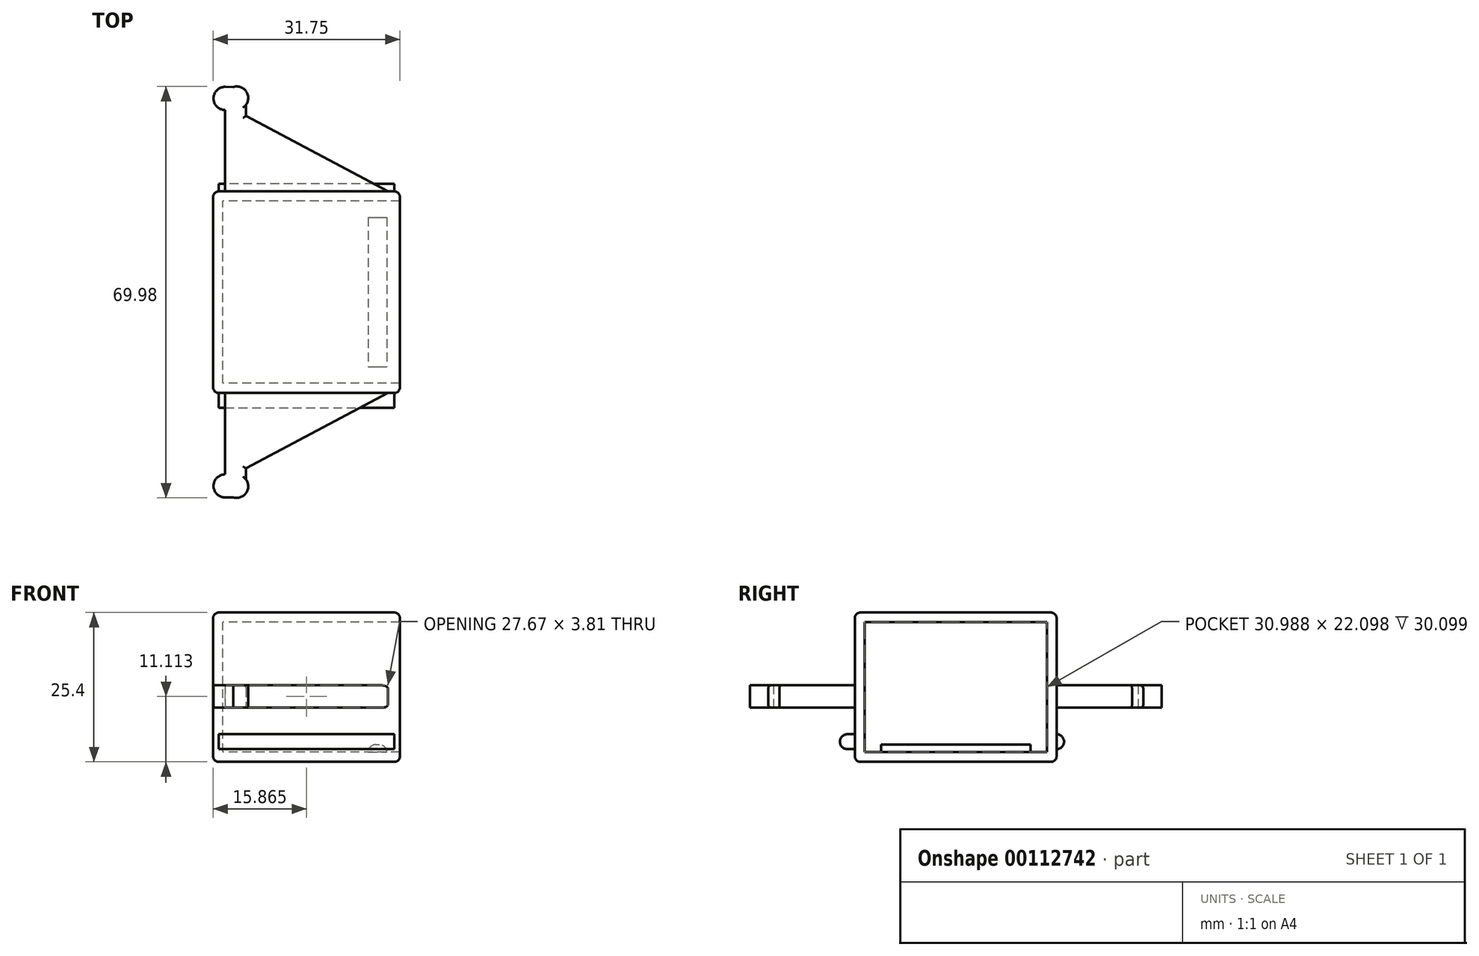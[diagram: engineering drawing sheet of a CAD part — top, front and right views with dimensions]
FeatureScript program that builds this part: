
annotation { "Feature Type Name" : "Feature", "Feature Type Description" : "" }
export const myFeature = defineFeature(function(context is Context, id is Id, definition is map)
    precondition{}
    {
        {
            var Q0;
            Q0=qCreatedBy(makeId("Right.planeOp"),FACE);
            var sketch = newSketch(context, id + "F0", { "sketchPlane" : qUnion([Q0])});
            skLineSegment(sketch, "E0.bottom", {"start": v(-17.14, 0) * mm, "end": v(17.15, 0) * mm});
            skLineSegment(sketch, "E0.top", {"start": v(-17.15, 25.4) * mm, "end": v(17.14, 25.4) * mm});
            skLineSegment(sketch, "E0.left", {"start": v(-17.14, 0) * mm, "end": v(-17.15, 25.4) * mm});
            skLineSegment(sketch, "E0.right", {"start": v(17.15, 0) * mm, "end": v(17.14, 25.4) * mm});
            skPoint(sketch, "E0.middle", {"position": v(0, 12.7) * mm});
            skLineSegment(sketch, "E1.0", {"start": v(16.26, 0.89) * mm, "end": v(16.26, 24.51) * mm, "construction": true});
            skLineSegment(sketch, "E1.1", {"start": v(-16.26, 0.89) * mm, "end": v(16.26, 0.89) * mm, "construction": true});
            skLineSegment(sketch, "E1.2", {"start": v(-16.26, 0.89) * mm, "end": v(-16.26, 24.51) * mm, "construction": true});
            skLineSegment(sketch, "E1.3", {"start": v(-16.26, 24.51) * mm, "end": v(16.26, 24.51) * mm, "construction": true});
            skSolve(sketch);
        }
        {
            var Q0;
            Q0=makeQuery(id+"F0.imprint","IMPRINT",FACE,{"disambiguationData":[TD([[makeQuery(id+"F0.imprint","IMPRINT",EDGE,{"derivedFrom":sQuery(id+"F0.wireOp",EDGE,"E1.0")}),1.0]])]});
            var Q1;
            Q1=makeQuery(id+"F0.imprint","IMPRINT",FACE,{"disambiguationData":[TD([[makeQuery(id+"F0.imprint","IMPRINT",EDGE,{"derivedFrom":sQuery(id+"F0.wireOp",EDGE,"E0.bottom")}),1.0]])]});
            extrude(context, id + "F1", {"entities" : qUnion([Q0, Q1]), "depth" : 31.75 * mm});
        }
        {
            var Q0;
            Q0=makeQuery(id+"F1.opExtrude","CAP_FACE",FACE,{"disambiguationData":[OSD([sQuery(id+"F0.wireOp",EDGE,"E0.bottom"),sQuery(id+"F0.wireOp",EDGE,"E0.top"),sQuery(id+"F0.wireOp",EDGE,"E0.left"),sQuery(id+"F0.wireOp",EDGE,"E0.right")])],"isStart":false});
            shell(context, id + "F2", {"entities" : qUnion([Q0]), "thickness" : 1.65 * mm});
        }
        {
            var Q0;
            Q0=qCreatedBy(makeId("Front.planeOp"),FACE);
            var sketch = newSketch(context, id + "F3", { "sketchPlane" : qUnion([Q0])});
            skCircle(sketch, "E2", {"center": v(12.7, 19.05) * mm, "radius": 2.38 * mm});
            skSolve(sketch);
        }
        {
            var Q0;
            Q0=makeQuery(id+"F1.opExtrude","SWEPT_EDGE",EDGE,{"disambiguationData":[OSD([sQuery(id+"F0.wireOp",EDGE,"E0.top"),sQuery(id+"F0.wireOp",EDGE,"E0.left")])]});
            var Q1;
            Q1=makeQuery(id+"F1.opExtrude","SWEPT_EDGE",EDGE,{"disambiguationData":[OSD([sQuery(id+"F0.wireOp",EDGE,"E0.bottom"),sQuery(id+"F0.wireOp",EDGE,"E0.left")])]});
            var Q2;
            Q2=makeQuery(id+"F1.opExtrude","SWEPT_EDGE",EDGE,{"disambiguationData":[OSD([sQuery(id+"F0.wireOp",EDGE,"E0.bottom"),sQuery(id+"F0.wireOp",EDGE,"E0.right")])]});
            var Q3;
            Q3=makeQuery(id+"F1.opExtrude","SWEPT_EDGE",EDGE,{"disambiguationData":[OSD([sQuery(id+"F0.wireOp",EDGE,"E0.top"),sQuery(id+"F0.wireOp",EDGE,"E0.right")])]});
            var Q4;
            Q4=makeQuery(id+"F1.opExtrude","CAP_EDGE",EDGE,{"disambiguationData":[OSD([sQuery(id+"F0.wireOp",EDGE,"E0.left")])],"isStart":true});
            var Q5;
            Q5=makeQuery(id+"F1.opExtrude","CAP_EDGE",EDGE,{"disambiguationData":[OSD([sQuery(id+"F0.wireOp",EDGE,"E0.bottom")])],"isStart":true});
            var Q6;
            Q6=makeQuery(id+"F1.opExtrude","CAP_EDGE",EDGE,{"disambiguationData":[OSD([sQuery(id+"F0.wireOp",EDGE,"E0.top")])],"isStart":true});
            var Q7;
            Q7=makeQuery(id+"F1.opExtrude","CAP_EDGE",EDGE,{"disambiguationData":[OSD([sQuery(id+"F0.wireOp",EDGE,"E0.right")])],"isStart":true});
            var Q8;
            Q8=makeQuery(id+"F1.opExtrude","CAP_EDGE",EDGE,{"disambiguationData":[OSD([sQuery(id+"F0.wireOp",EDGE,"E0.top")])],"isStart":false});
            var Q9;
            Q9=makeQuery(id+"F1.opExtrude","CAP_EDGE",EDGE,{"disambiguationData":[OSD([sQuery(id+"F0.wireOp",EDGE,"E0.left")])],"isStart":false});
            var Q10;
            Q10=makeQuery(id+"F1.opExtrude","CAP_EDGE",EDGE,{"disambiguationData":[OSD([sQuery(id+"F0.wireOp",EDGE,"E0.right")])],"isStart":false});
            var Q11;
            Q11=makeQuery(id+"F1.opExtrude","CAP_EDGE",EDGE,{"disambiguationData":[OSD([sQuery(id+"F0.wireOp",EDGE,"E0.bottom")])],"isStart":false});
            fillet(context, id + "F4", {"entities" : qUnion([Q0, Q1, Q2, Q3, Q4, Q5, Q6, Q7, Q8, Q9, Q10, Q11]), "radius" : 0.95 * mm, "tangentPropagation" : true, "allowEdgeOverflow" : false});
        }
        {
            var Q0;
            Q0=qCreatedBy(makeId("Top.planeOp"),FACE);
            cPlane(context, id + "F5", {"entities" : qUnion([Q0]), "cplaneType" : CPlaneType.OFFSET, "offset" : 11.1 * mm, "width" : 152.4 * mm, "height" : 152.4 * mm});
        }
        {
            var Q0;
            Q0=qCreatedBy(id+"F5.planeOp",FACE);
            var sketch = newSketch(context, id + "F6", { "sketchPlane" : qUnion([Q0])});
            skLineSegment(sketch, "E3", {"start": v(28.23, 0) * mm, "end": v(-2.77, 0) * mm, "construction": true});
            skLineSegment(sketch, "E4", {"start": v(2.03, 17.14) * mm, "end": v(2.03, 32.96) * mm});
            skLineSegment(sketch, "E5", {"start": v(5.59, 29.96) * mm, "end": v(5.59, 31.87) * mm});
            skArc(sketch, "E6", {"start": v(5.59, 31.87) * mm, "mid": v(4.57, 34.9) * mm, "end": v(2.03, 32.96) * mm});
            skLineSegment(sketch, "E7", {"start": v(5.59, 29.96) * mm, "end": v(29.7, 17.14) * mm});
            skLineSegment(sketch, "E8", {"start": v(29.7, 17.15) * mm, "end": v(2.03, 17.14) * mm});
            skCircle(sketch, "E9", {"center": v(2.03, 32.96) * mm, "radius": 1.97 * mm});
            skLineSegment(sketch, "E10", {"start": v(2.03, 34.92) * mm, "end": v(4.57, 34.9) * mm});
            skArc(sketch, "E11.MirrorCS", {"start": v(5.59, -31.87) * mm, "mid": v(4.57, -34.9) * mm, "end": v(2.03, -32.96) * mm});
            skCircle(sketch, "E12.MirrorC", {"center": v(2.03, -32.96) * mm, "radius": 1.97 * mm});
            skLineSegment(sketch, "E13.MirrorCS", {"start": v(2.03, -17.14) * mm, "end": v(2.03, -32.96) * mm});
            skLineSegment(sketch, "E14.MirrorCS", {"start": v(5.59, -29.96) * mm, "end": v(5.59, -31.87) * mm});
            skLineSegment(sketch, "E15.MirrorCS", {"start": v(5.59, -29.96) * mm, "end": v(29.7, -17.15) * mm});
            skLineSegment(sketch, "E16.MirrorCS", {"start": v(29.7, -17.15) * mm, "end": v(2.03, -17.14) * mm});
            skLineSegment(sketch, "E17.MirrorCS", {"start": v(2.03, -34.92) * mm, "end": v(4.57, -34.9) * mm});
            skSolve(sketch);
        }
        {
            var Q0;
            Q0 = qSketchRegion(id + "F6", true);
            extrude(context, id + "F7", {"entities" : qUnion([Q0]), "operationType" : NewBodyOperationType.ADD, "depth" : 3.8 * mm, "symmetric" : true});
        }
        {
            var Q0;
            Q0=makeQuery(id+"F7.opExtrude","CAP_EDGE",EDGE,{"disambiguationData":[OSD([sQuery(id+"F6.wireOp",EDGE,"E15.MirrorCS")])],"isStart":false});
            var Q1;
            Q1=makeQuery(id+"F7.opExtrude","CAP_EDGE",EDGE,{"disambiguationData":[OSD([sQuery(id+"F6.wireOp",EDGE,"E7")])],"isStart":false});
            var Q2;
            Q2=makeQuery(id+"F7.opExtrude","CAP_EDGE",EDGE,{"disambiguationData":[OSD([sQuery(id+"F6.wireOp",EDGE,"E15.MirrorCS")])],"isStart":true});
            var Q3;
            Q3=makeQuery(id+"F7.opExtrude","CAP_EDGE",EDGE,{"disambiguationData":[OSD([sQuery(id+"F6.wireOp",EDGE,"E7")])],"isStart":true});
            var Q4;
            Q4=makeQuery(id+"F7.opExtrude","CAP_EDGE",EDGE,{"disambiguationData":[OSD([sQuery(id+"F6.wireOp",EDGE,"E5")])],"isStart":false});
            var Q5;
            Q5=makeQuery(id+"F7.opExtrude","CAP_EDGE",EDGE,{"disambiguationData":[OSD([sQuery(id+"F6.wireOp",EDGE,"E5")])],"isStart":true});
            var Q6;
            Q6=makeQuery(id+"F7.opExtrude","CAP_EDGE",EDGE,{"disambiguationData":[OSD([sQuery(id+"F6.wireOp",EDGE,"E14.MirrorCS")])],"isStart":false});
            var Q7;
            Q7=makeQuery(id+"F7.opExtrude","CAP_EDGE",EDGE,{"disambiguationData":[OSD([sQuery(id+"F6.wireOp",EDGE,"E14.MirrorCS")])],"isStart":true});
            fillet(context, id + "F8", {"entities" : qUnion([Q0, Q1, Q2, Q3, Q4, Q5, Q6, Q7]), "radius" : 0.5 * mm, "tangentPropagation" : true, "allowEdgeOverflow" : false});
        }
        {
            var Q0;
            Q0=makeQuery(id+"F2.opShell","OFFSET_FACE",FACE,{"disambiguationData":[OSD([sQuery(id+"F0.wireOp",EDGE,"E0.bottom")])]});
            cPlane(context, id + "F9", {"entities" : qUnion([Q0]), "cplaneType" : CPlaneType.OFFSET, "offset" : 0 * mm, "width" : 152.4 * mm, "height" : 152.4 * mm});
        }
        {
            var Q0;
            Q0=qCreatedBy(id+"F9.planeOp",FACE);
            var sketch = newSketch(context, id + "F10", { "sketchPlane" : qUnion([Q0])});
            skLineSegment(sketch, "E18.bottom", {"start": v(26.35, 12.7) * mm, "end": v(29.53, 12.7) * mm});
            skLineSegment(sketch, "E18.top", {"start": v(26.35, -12.7) * mm, "end": v(29.53, -12.7) * mm});
            skLineSegment(sketch, "E18.left", {"start": v(26.35, 12.7) * mm, "end": v(26.35, -12.7) * mm});
            skLineSegment(sketch, "E18.right", {"start": v(29.53, 12.7) * mm, "end": v(29.53, -12.7) * mm});
            skPoint(sketch, "E18.middle", {"position": v(27.94, 0) * mm});
            skSolve(sketch);
        }
        {
            var Q0;
            Q0 = qSketchRegion(id + "F10", true);
            extrude(context, id + "F11", {"entities" : qUnion([Q0]), "operationType" : NewBodyOperationType.ADD, "depth" : 1.27 * mm});
        }
        {
            var Q0;
            Q0=makeQuery(id+"F11.opExtrude","CAP_EDGE",EDGE,{"disambiguationData":[OSD([sQuery(id+"F10.wireOp",EDGE,"E18.right")])],"isStart":false});
            var Q1;
            Q1=makeQuery(id+"F11.opExtrude","CAP_EDGE",EDGE,{"disambiguationData":[OSD([sQuery(id+"F10.wireOp",EDGE,"E18.left")])],"isStart":false});
            fillet(context, id + "F12", {"entities" : qUnion([Q0, Q1]), "radius" : 1.27 * mm, "tangentPropagation" : true, "allowEdgeOverflow" : false});
        }
        {
            var Q0;
            Q0=makeQuery(id+"F1.opExtrude","SWEPT_FACE",FACE,{"disambiguationData":[OSD([sQuery(id+"F0.wireOp",EDGE,"E0.left")])]});
            cPlane(context, id + "F13", {"entities" : qUnion([Q0]), "cplaneType" : CPlaneType.OFFSET, "offset" : 0 * mm, "width" : 152.4 * mm, "height" : 152.4 * mm});
        }
        {
            var Q0;
            Q0=qCreatedBy(id+"F13.planeOp",FACE);
            var sketch = newSketch(context, id + "F14", { "sketchPlane" : qUnion([Q0])});
            skLineSegment(sketch, "E19.bottom", {"start": v(0.95, 4.7) * mm, "end": v(30.8, 4.7) * mm});
            skLineSegment(sketch, "E19.top", {"start": v(0.95, 2.16) * mm, "end": v(30.8, 2.16) * mm});
            skLineSegment(sketch, "E19.left", {"start": v(0.95, 4.7) * mm, "end": v(0.95, 2.16) * mm});
            skLineSegment(sketch, "E19.right", {"start": v(30.8, 4.7) * mm, "end": v(30.8, 2.16) * mm});
            skSolve(sketch);
        }
        {
            var Q0;
            Q0 = qSketchRegion(id + "F14", true);
            extrude(context, id + "F15", {"entities" : qUnion([Q0]), "operationType" : NewBodyOperationType.ADD, "depth" : 2.54 * mm});
        }
        {
            var Q0;
            Q0=makeQuery(id+"F1.opExtrude","SWEPT_FACE",FACE,{"disambiguationData":[OSD([sQuery(id+"F0.wireOp",EDGE,"E0.right")])]});
            cPlane(context, id + "F16", {"entities" : qUnion([Q0]), "cplaneType" : CPlaneType.OFFSET, "offset" : 0 * mm, "width" : 152.4 * mm, "height" : 152.4 * mm});
        }
        {
            var Q0;
            Q0=qCreatedBy(id+"F16.planeOp",FACE);
            var sketch = newSketch(context, id + "F17", { "sketchPlane" : qUnion([Q0])});
            skLineSegment(sketch, "E20.bottom", {"start": v(-30.8, 4.7) * mm, "end": v(-0.95, 4.7) * mm});
            skLineSegment(sketch, "E20.top", {"start": v(-30.8, 2.16) * mm, "end": v(-0.95, 2.16) * mm});
            skLineSegment(sketch, "E20.left", {"start": v(-30.8, 4.7) * mm, "end": v(-30.8, 2.16) * mm});
            skLineSegment(sketch, "E20.right", {"start": v(-0.95, 4.7) * mm, "end": v(-0.95, 2.16) * mm});
            skSolve(sketch);
        }
        {
            var Q0;
            Q0 = qSketchRegion(id + "F17", true);
            extrude(context, id + "F18", {"entities" : qUnion([Q0]), "operationType" : NewBodyOperationType.ADD, "depth" : 1.27 * mm});
        }
        {
            var Q0;
            Q0=makeQuery(id+"F18.opExtrude","CAP_EDGE",EDGE,{"disambiguationData":[OSD([sQuery(id+"F17.wireOp",EDGE,"E20.bottom")])],"isStart":false});
            var Q1;
            Q1=makeQuery(id+"F18.opExtrude","CAP_EDGE",EDGE,{"disambiguationData":[OSD([sQuery(id+"F17.wireOp",EDGE,"E20.top")])],"isStart":false});
            var Q2;
            Q2=makeQuery(id+"F15.opExtrude","CAP_EDGE",EDGE,{"disambiguationData":[OSD([sQuery(id+"F14.wireOp",EDGE,"E19.bottom")])],"isStart":false});
            var Q3;
            Q3=makeQuery(id+"F15.opExtrude","CAP_EDGE",EDGE,{"disambiguationData":[OSD([sQuery(id+"F14.wireOp",EDGE,"E19.top")])],"isStart":false});
            fillet(context, id + "F19", {"entities" : qUnion([Q0, Q1, Q2, Q3]), "radius" : 1.27 * mm, "tangentPropagation" : true, "allowEdgeOverflow" : false});
        }
    });
